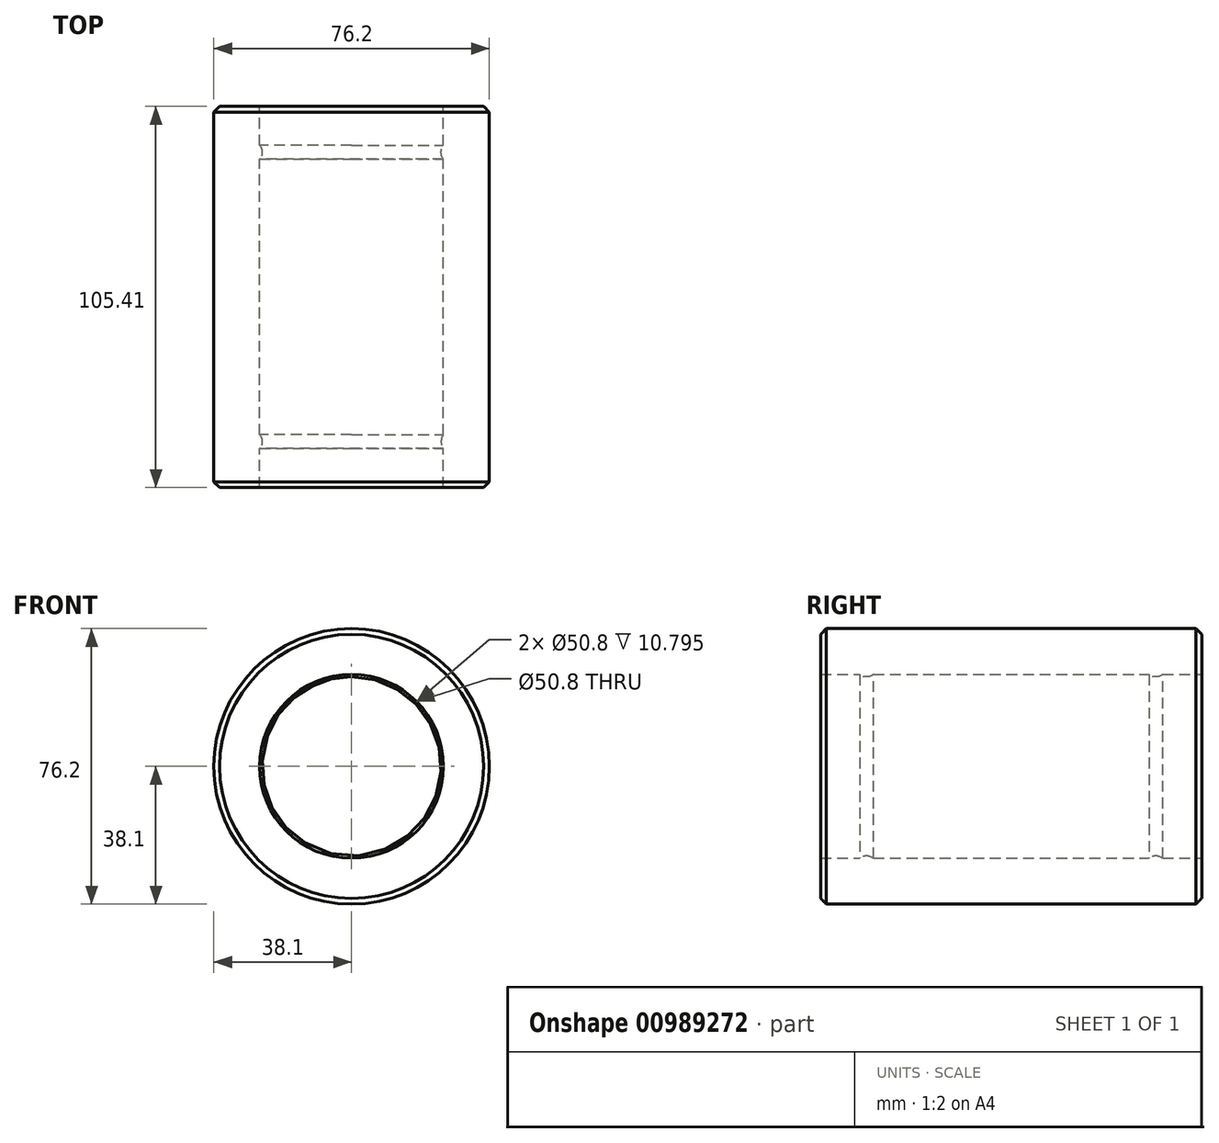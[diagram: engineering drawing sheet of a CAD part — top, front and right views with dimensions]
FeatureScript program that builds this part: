
annotation { "Feature Type Name" : "Feature", "Feature Type Description" : "" }
export const myFeature = defineFeature(function(context is Context, id is Id, definition is map)
    precondition{}
    {
        {
            var Q0;
            Q0=qCreatedBy(makeId("Front.planeOp"),FACE);
            var sketch = newSketch(context, id + "F0", { "sketchPlane" : qUnion([Q0])});
            skCircle(sketch, "E0", {"center": v(0, 0) * mm, "radius": 38.1 * mm});
            skCircle(sketch, "E1", {"center": v(0, 0) * mm, "radius": 25.4 * mm});
            skSolve(sketch);
        }
        {
            var Q0;
            Q0 = qSketchRegion(id + "F0", true);
            extrude(context, id + "F1", {"entities" : qUnion([Q0]), "depth" : 105.4 * mm, "offsetDistance" : 25.4 * mm});
        }
        {
            var Q0;
            Q0=qCreatedBy(makeId("Top.planeOp"),FACE);
            var sketch = newSketch(context, id + "F2", { "sketchPlane" : qUnion([Q0])});
            skCircle(sketch, "E2", {"center": v(-27.94, -92.71) * mm, "radius": 3.17 * mm});
            skLineSegment(sketch, "E3", {"start": v(38.1, 0) * mm, "end": v(38.1, -105.41) * mm});
            skLineSegment(sketch, "E4", {"start": v(38.1, -52.7) * mm, "end": v(-40.57, -52.7) * mm});
            skCircle(sketch, "E5.MirrorC", {"center": v(-27.94, -12.7) * mm, "radius": 3.17 * mm});
            skSolve(sketch);
        }
        {
            var Q0;
            Q0 = qSketchRegion(id + "F2", true);
            var Q1;
            Q1=makeQuery(id+"F1.opExtrude","CAP_EDGE",EDGE,{"disambiguationData":[OSD([sQuery(id+"F0.wireOp",EDGE,"E0")])],"isStart":false});
            revolve(context, id + "F3", {"operationType" : NewBodyOperationType.ADD, "surfaceOperationType" : NewSurfaceOperationType.NEW, "entities" : qUnion([Q0]), "axis" : qUnion([Q1]), "revolveType" : RevolveType.FULL});
        }
        {
            var Q0;
            Q0=makeQuery(id+"F1.opExtrude","CAP_EDGE",EDGE,{"disambiguationData":[OSD([sQuery(id+"F0.wireOp",EDGE,"E0")])],"isStart":false});
            var Q1;
            Q1=makeQuery(id+"F1.opExtrude","CAP_EDGE",EDGE,{"disambiguationData":[OSD([sQuery(id+"F0.wireOp",EDGE,"E0")])],"isStart":true});
            chamfer(context, id + "F4", {"entities" : qUnion([Q0, Q1]), "width" : 1.6 * mm, "tangentPropagation" : true});
        }
    });
